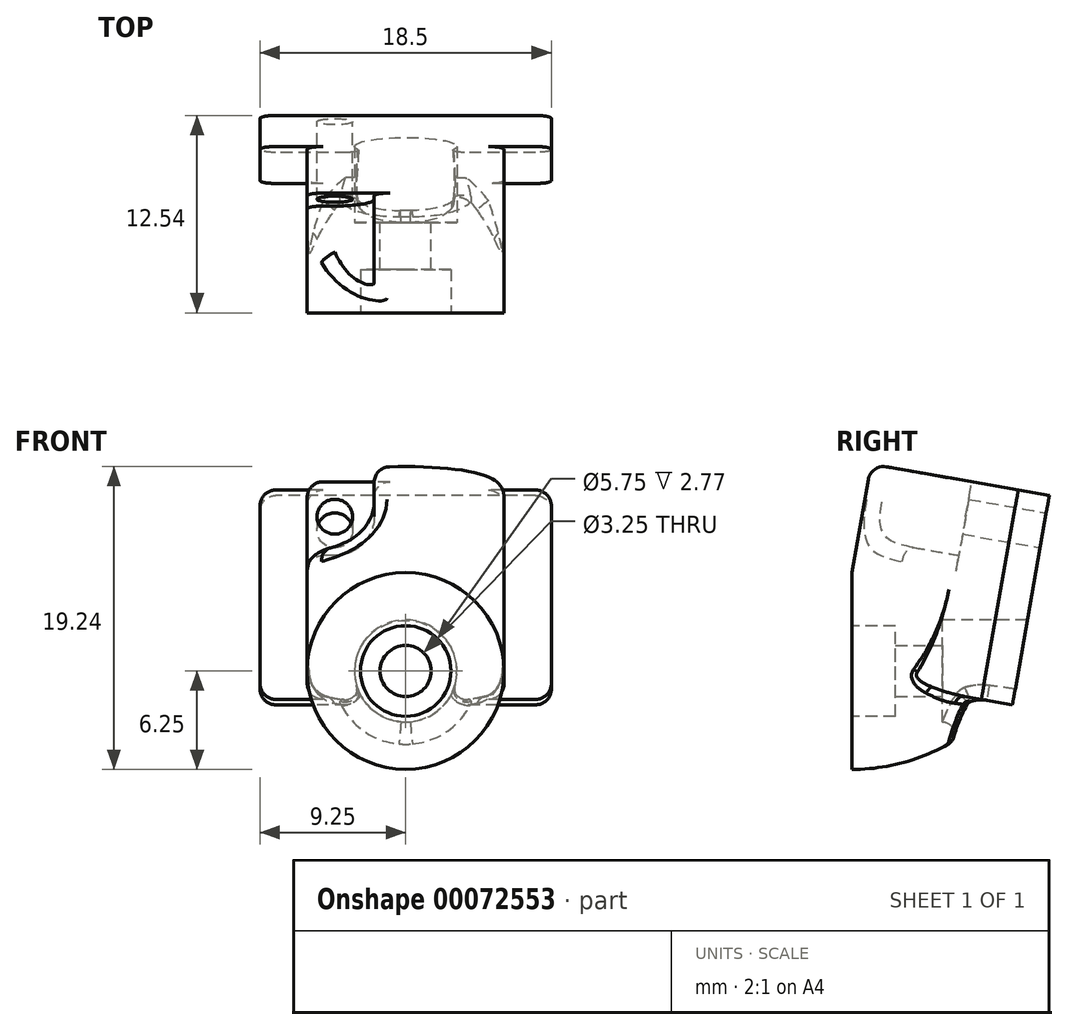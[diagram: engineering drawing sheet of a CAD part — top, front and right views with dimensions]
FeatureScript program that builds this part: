
annotation { "Feature Type Name" : "Feature", "Feature Type Description" : "" }
export const myFeature = defineFeature(function(context is Context, id is Id, definition is map)
    precondition{}
    {
        {
            var Q0;
            Q0=qCreatedBy(makeId("Front.planeOp"),FACE);
            var sketch = newSketch(context, id + "F0", { "sketchPlane" : qUnion([Q0])});
            skCircle(sketch, "E0", {"center": v(0, 0) * mm, "radius": 6.25 * mm});
            skSolve(sketch);
        }
        {
            var Q0;
            Q0=qCreatedBy(makeId("Front.planeOp"),FACE);
            var sketch = newSketch(context, id + "F1", { "sketchPlane" : qUnion([Q0])});
            skLineSegment(sketch, "E1", {"start": v(-10, 6.25) * mm, "end": v(10, 6.25) * mm, "construction": true});
            skLineSegment(sketch, "E2", {"start": v(-10, 6.25) * mm, "end": v(0, 0) * mm, "construction": true});
            skLineSegment(sketch, "E3", {"start": v(0, 0) * mm, "end": v(10, 6.25) * mm, "construction": true});
            skSolve(sketch);
        }
        {
            var Q0;
            Q0=makeQuery(id+"F0.imprint","IMPRINT",FACE,{"disambiguationData":[TD([[makeQuery(id+"F0.imprint","IMPRINT",EDGE,{"derivedFrom":sQuery(id+"F0.wireOp",EDGE,"E0")}),1.0]])]});
            var Q1;
            Q1=sQuery(id+"F1.wireOp",EDGE,"E1");
            revolve(context, id + "F2", {"entities" : qUnion([Q0]), "axis" : qUnion([Q1]), "revolveType" : RevolveType.ONE_DIRECTION, "angle" : 80 * degree});
        }
        {
            var Q0;
            Q0=makeQuery(id+"F2.opRevolve","CAP_FACE",FACE,{"disambiguationData":[OSD([sQuery(id+"F0.wireOp",EDGE,"E0")])],"isStart":false});
            var sketch = newSketch(context, id + "F3", { "sketchPlane" : qUnion([Q0])});
            skCircle(sketch, "E4.0.0", {"center": v(0, 5.16) * mm, "radius": 6.25 * mm});
            skSolve(sketch);
        }
        {
            var Q0;
            Q0=qSketchRegion(id+"F3",true);
            extrude(context, id + "F4", {"entities" : qUnion([Q0]), "operationType" : NewBodyOperationType.ADD, "depth" : 7 * mm});
        }
        {
            var Q0;
            Q0=makeQuery(id+"F4.opExtrude","CAP_FACE",FACE,{"disambiguationData":[OSD([sQuery(id+"F3.wireOp",EDGE,"E4.0.0")])],"isStart":false});
            var sketch = newSketch(context, id + "F5", { "sketchPlane" : qUnion([Q0])});
            skLineSegment(sketch, "E5.bottom", {"start": v(9.25, 8.41) * mm, "end": v(6.25, 8.41) * mm});
            skLineSegment(sketch, "E5.top", {"start": v(9.25, 10.41) * mm, "end": v(-9.25, 10.41) * mm});
            skLineSegment(sketch, "E5.left", {"start": v(9.25, 8.41) * mm, "end": v(9.25, 10.41) * mm});
            skLineSegment(sketch, "E5.right", {"start": v(-9.25, 8.41) * mm, "end": v(-9.25, 10.41) * mm});
            skLineSegment(sketch, "E6.left", {"start": v(6.25, 8.41) * mm, "end": v(6.25, 5.16) * mm});
            skLineSegment(sketch, "E6.right", {"start": v(-6.25, 8.41) * mm, "end": v(-6.25, 5.16) * mm});
            skArc(sketch, "E7", {"start": v(6.25, 5.16) * mm, "mid": v(0, -1.09) * mm, "end": v(-6.25, 5.16) * mm});
            skLineSegment(sketch, "E8.trimOffspring", {"start": v(-6.25, 8.41) * mm, "end": v(-9.25, 8.41) * mm});
            skSolve(sketch);
        }
        {
            var Q0;
            Q0=qSketchRegion(id+"F5",true);
            extrude(context, id + "F6", {"entities" : qUnion([Q0]), "operationType" : NewBodyOperationType.ADD, "oppositeDirection" : true, "depth" : 13.5 * mm});
        }
        {
            var Q0;
            {var subQ4=sQuery(id+"F5.wireOp",EDGE,"E5.right");var subQ6=sQuery(id+"F5.wireOp",EDGE,"E5.top");Q0=makeQuery(id+"F6.boolean.opBoolean","SPLIT",FACE,{"disambiguationData":[TD([makeQuery(id+"F6.opExtrude","SWEPT_FACE",FACE,{"disambiguationData":[OSD([subQ4])]})])],"derivedFrom":makeQuery(id+"F6.opExtrude","SWEPT_FACE",FACE,{"disambiguationData":[OSD([subQ6])]})});}
            var sketch = newSketch(context, id + "F7", { "sketchPlane" : qUnion([Q0])});
            skLineSegment(sketch, "E9.bottom", {"start": v(-20, 16.1) * mm, "end": v(22.94, 16.1) * mm});
            skLineSegment(sketch, "E9.top", {"start": v(-20, -5.87) * mm, "end": v(22.94, -5.87) * mm});
            skLineSegment(sketch, "E9.left", {"start": v(-20, 16.1) * mm, "end": v(-20, -5.87) * mm});
            skLineSegment(sketch, "E9.right", {"start": v(22.94, 16.1) * mm, "end": v(22.94, -5.87) * mm});
            skSolve(sketch);
        }
        {
            var Q0;
            Q0 = qSketchRegion(id + "F7", true);
            extrude(context, id + "F8", {"entities" : qUnion([Q0]), "operationType" : NewBodyOperationType.REMOVE, "depth" : 25 * mm});
        }
        {
            var Q0;
            Q0=makeQuery(id+"F2.opRevolve","CAP_FACE",FACE,{"disambiguationData":[OSD([sQuery(id+"F0.wireOp",EDGE,"E0")])],"isStart":true});
            var sketch = newSketch(context, id + "F9", { "sketchPlane" : qUnion([Q0])});
            skCircle(sketch, "E10.0", {"center": v(0, 0) * mm, "radius": 6.25 * mm});
            skSolve(sketch);
        }
        {
            var Q0;
            Q0=qSketchRegion(id+"F9",true);
            extrude(context, id + "F10", {"entities" : qUnion([Q0]), "operationType" : NewBodyOperationType.REMOVE, "depth" : 25 * mm});
        }
        {
            var Q0;
            Q0=makeQuery(id+"F6.opExtrude","SWEPT_FACE",FACE,{"disambiguationData":[OSD([sQuery(id+"F5.wireOp",EDGE,"E5.top")])]});
            var sketch = newSketch(context, id + "F11", { "sketchPlane" : qUnion([Q0])});
            skCircle(sketch, "E11", {"center": v(-4.5, 10.9) * mm, "radius": 1.13 * mm, "construction": true});
            skEllipse(sketch, "E12.0", {"center": v(0, 0) * mm, "majorRadius": 6.25 * mm, "minorRadius": 6.16 * mm, "majorAxis": v(-1, 0), "construction": true});
            skLineSegment(sketch, "E13", {"start": v(0, 0) * mm, "end": v(0, 18.18) * mm, "construction": true});
            skCircle(sketch, "E14.MirrorC", {"center": v(4.5, 10.9) * mm, "radius": 1.13 * mm});
            skSolve(sketch);
        }
        {
            var Q0;
            Q0=qSketchRegion(id+"F11",true);
            extrude(context, id + "F12", {"entities" : qUnion([Q0]), "operationType" : NewBodyOperationType.REMOVE, "oppositeDirection" : true, "depth" : 25 * mm});
        }
        {
            var Q0;
            Q0=makeQuery(id+"F10.boolean.opBoolean","MERGE",FACE,{"derivedFrom":[makeQuery(id+"F2.opRevolve","CAP_FACE",FACE,{"disambiguationData":[OSD([sQuery(id+"F0.wireOp",EDGE,"E0")])],"isStart":true}),makeQuery(id+"F10.opExtrude","CAP_FACE",FACE,{"disambiguationData":[OSD([sQuery(id+"F9.wireOp",EDGE,"E10.0")])],"isStart":true})]});
            var sketch = newSketch(context, id + "F13", { "sketchPlane" : qUnion([Q0])});
            skCircle(sketch, "E15", {"center": v(0, 0) * mm, "radius": 2.87 * mm});
            skSolve(sketch);
        }
        {
            var Q0;
            Q0=qSketchRegion(id+"F13",true);
            extrude(context, id + "F14", {"entities" : qUnion([Q0]), "operationType" : NewBodyOperationType.REMOVE, "oppositeDirection" : true, "depth" : 2.77 * mm});
        }
        {
            var Q0;
            Q0=makeQuery(id+"F10.boolean.opBoolean","MERGE",FACE,{"derivedFrom":[makeQuery(id+"F2.opRevolve","CAP_FACE",FACE,{"disambiguationData":[OSD([sQuery(id+"F0.wireOp",EDGE,"E0")])],"isStart":true}),makeQuery(id+"F10.opExtrude","CAP_FACE",FACE,{"disambiguationData":[OSD([sQuery(id+"F9.wireOp",EDGE,"E10.0")])],"isStart":true})]});
            cPlane(context, id + "F15", {"entities" : qUnion([Q0]), "cplaneType" : CPlaneType.OFFSET, "offset" : 5.75 * mm, "oppositeDirection" : true, "width" : 150 * mm, "height" : 150 * mm});
        }
        {
            var Q0;
            Q0=qCreatedBy(id+"F15.planeOp",FACE);
            var sketch = newSketch(context, id + "F16", { "sketchPlane" : qUnion([Q0])});
            skCircle(sketch, "E16", {"center": v(0, 0) * mm, "radius": 3.25 * mm});
            skSolve(sketch);
        }
        {
            var Q0;
            Q0=makeQuery(id+"F10.boolean.opBoolean","MERGE",FACE,{"derivedFrom":[makeQuery(id+"F2.opRevolve","CAP_FACE",FACE,{"disambiguationData":[OSD([sQuery(id+"F0.wireOp",EDGE,"E0")])],"isStart":true}),makeQuery(id+"F10.opExtrude","CAP_FACE",FACE,{"disambiguationData":[OSD([sQuery(id+"F9.wireOp",EDGE,"E10.0")])],"isStart":true})]});
            var sketch = newSketch(context, id + "F17", { "sketchPlane" : qUnion([Q0])});
            skLineSegment(sketch, "E17", {"start": v(0, 6.25) * mm, "end": v(16.38, 6.25) * mm});
            skSolve(sketch);
        }
        {
            var Q0;
            Q0=makeQuery(id+"F6.opExtrude","SWEPT_FACE",FACE,{"disambiguationData":[OSD([sQuery(id+"F5.wireOp",EDGE,"E5.top")])]});
            cPlane(context, id + "F18", {"entities" : qUnion([Q0]), "cplaneType" : CPlaneType.OFFSET, "offset" : 5 * mm, "oppositeDirection" : true, "width" : 150 * mm, "height" : 150 * mm});
        }
        {
            var Q0;
            Q0=qCreatedBy(id+"F18.planeOp",FACE);
            var sketch = newSketch(context, id + "F19", { "sketchPlane" : qUnion([Q0])});
            skArc(sketch, "E18", {"start": v(-4.5, 8.4) * mm, "mid": v(-2.73, 9.14) * mm, "end": v(-2, 10.9) * mm, "construction": true});
            skLineSegment(sketch, "E19.bottom", {"start": v(-4.5, 8.4) * mm, "end": v(-12.7, 8.4) * mm, "construction": true});
            skLineSegment(sketch, "E19.top", {"start": v(-2, 17.18) * mm, "end": v(-12.7, 17.18) * mm, "construction": true});
            skLineSegment(sketch, "E19.left", {"start": v(-2, 10.9) * mm, "end": v(-2, 17.18) * mm, "construction": true});
            skLineSegment(sketch, "E19.right", {"start": v(-12.7, 8.4) * mm, "end": v(-12.7, 17.18) * mm, "construction": true});
            skEllipse(sketch, "E20.0", {"center": v(0, 0) * mm, "majorRadius": 2.87 * mm, "minorRadius": 2.83 * mm, "majorAxis": v(-1, 0), "construction": true});
            skLineSegment(sketch, "E21", {"start": v(0, 0) * mm, "end": v(0, 16.32) * mm, "construction": true});
            skLineSegment(sketch, "E22.MirrorCS", {"start": v(12.7, 8.4) * mm, "end": v(12.7, 17.18) * mm});
            skLineSegment(sketch, "E23.MirrorCS", {"start": v(2, 10.9) * mm, "end": v(2, 17.18) * mm});
            skLineSegment(sketch, "E24.MirrorCS", {"start": v(2, 17.18) * mm, "end": v(12.7, 17.18) * mm});
            skLineSegment(sketch, "E25.MirrorCS", {"start": v(4.5, 8.4) * mm, "end": v(12.7, 8.4) * mm});
            skArc(sketch, "E26.MirrorCS", {"start": v(4.5, 8.4) * mm, "mid": v(2.73, 9.14) * mm, "end": v(2, 10.9) * mm});
            skSolve(sketch);
        }
        {
            var Q0;
            Q0=qSketchRegion(id+"F19",true);
            extrude(context, id + "F20", {"entities" : qUnion([Q0]), "operationType" : NewBodyOperationType.REMOVE, "oppositeDirection" : true, "depth" : 25 * mm});
        }
        {
            var Q0;
            Q0=makeQuery(id+"F20.boolean.opBoolean","INTERSECT",EDGE,{"derivedFrom":[makeQuery(id+"F6.boolean.opBoolean","MERGE",FACE,{"derivedFrom":[makeQuery(id+"F4.opExtrude","CAP_FACE",FACE,{"disambiguationData":[OSD([sQuery(id+"F3.wireOp",EDGE,"E4.0.0")])],"isStart":false}),makeQuery(id+"F6.opExtrude","CAP_FACE",FACE,{"disambiguationData":[OSD([sQuery(id+"F5.wireOp",EDGE,"E5.bottom"),sQuery(id+"F5.wireOp",EDGE,"E5.top"),sQuery(id+"F5.wireOp",EDGE,"E5.left"),sQuery(id+"F5.wireOp",EDGE,"E5.right"),sQuery(id+"F5.wireOp",EDGE,"E6.left"),sQuery(id+"F5.wireOp",EDGE,"E6.right"),sQuery(id+"F5.wireOp",EDGE,"E7"),sQuery(id+"F5.wireOp",EDGE,"E8.trimOffspring")])],"isStart":true})]}),makeQuery(id+"F20.opExtrude","SWEPT_FACE",FACE,{"disambiguationData":[OSD([sQuery(id+"F19.wireOp",EDGE,"E23.MirrorCS")])]})]});
            var Q1;
            Q1=makeQuery(id+"F6.opExtrude","CAP_EDGE",EDGE,{"disambiguationData":[OSD([sQuery(id+"F5.wireOp",EDGE,"E6.left")])],"isStart":true});
            var Q2;
            {var subQ3=sQuery(id+"F3.wireOp",EDGE,"E4.0.0");var subQ4=sQuery(id+"F0.wireOp",EDGE,"E0");Q2=makeQuery(id+"F20.boolean.opBoolean","INTERSECT",EDGE,{"derivedFrom":[makeQuery(id+"F6.boolean.opBoolean","SPLIT",FACE,{"disambiguationData":[TD([makeQuery(id+"F2.opRevolve","CAP_FACE",FACE,{"disambiguationData":[OSD([subQ4])],"isStart":true})])],"derivedFrom":makeQuery(id+"F4.opExtrude","SWEPT_FACE",FACE,{"disambiguationData":[OSD([subQ3])]})}),makeQuery(id+"F20.opExtrude","SWEPT_FACE",FACE,{"disambiguationData":[OSD([sQuery(id+"F19.wireOp",EDGE,"E26.MirrorCS")])]})]});}
            var Q3;
            {var subQ3=sQuery(id+"F3.wireOp",EDGE,"E4.0.0");var subQ4=sQuery(id+"F0.wireOp",EDGE,"E0");Q3=makeQuery(id+"F20.boolean.opBoolean","INTERSECT",EDGE,{"derivedFrom":[makeQuery(id+"F6.boolean.opBoolean","SPLIT",FACE,{"disambiguationData":[TD([makeQuery(id+"F2.opRevolve","CAP_FACE",FACE,{"disambiguationData":[OSD([subQ4])],"isStart":true})])],"derivedFrom":makeQuery(id+"F4.opExtrude","SWEPT_FACE",FACE,{"disambiguationData":[OSD([subQ3])]})}),makeQuery(id+"F20.opExtrude","SWEPT_FACE",FACE,{"disambiguationData":[OSD([sQuery(id+"F19.wireOp",EDGE,"E23.MirrorCS")])]})]});}
            var Q4;
            {var subQ3=sQuery(id+"F3.wireOp",EDGE,"E4.0.0");var subQ4=sQuery(id+"F0.wireOp",EDGE,"E0");Q4=makeQuery(id+"F20.boolean.opBoolean","INTERSECT",EDGE,{"derivedFrom":[makeQuery(id+"F6.boolean.opBoolean","SPLIT",FACE,{"disambiguationData":[TD([makeQuery(id+"F2.opRevolve","CAP_FACE",FACE,{"disambiguationData":[OSD([subQ4])],"isStart":true})])],"derivedFrom":makeQuery(id+"F4.opExtrude","SWEPT_FACE",FACE,{"disambiguationData":[OSD([subQ3])]})}),makeQuery(id+"F20.opExtrude","SWEPT_FACE",FACE,{"disambiguationData":[OSD([sQuery(id+"F19.wireOp",EDGE,"E25.MirrorCS")])]})]});}
            var Q5;
            Q5=makeQuery(id+"F6.opExtrude","CAP_EDGE",EDGE,{"disambiguationData":[OSD([sQuery(id+"F5.wireOp",EDGE,"E5.right")])],"isStart":true});
            var Q6;
            Q6=makeQuery(id+"F6.opExtrude","CAP_EDGE",EDGE,{"disambiguationData":[OSD([sQuery(id+"F5.wireOp",EDGE,"E5.left")])],"isStart":true});
            var Q7;
            Q7=makeQuery(id+"F6.opExtrude","CAP_EDGE",EDGE,{"disambiguationData":[OSD([sQuery(id+"F5.wireOp",EDGE,"E6.right")])],"isStart":false});
            var Q8;
            Q8=makeQuery(id+"F6.opExtrude","CAP_EDGE",EDGE,{"disambiguationData":[OSD([sQuery(id+"F5.wireOp",EDGE,"E6.left")])],"isStart":false});
            var Q9;
            Q9=makeQuery(id+"F6.opExtrude","CAP_EDGE",EDGE,{"disambiguationData":[OSD([sQuery(id+"F5.wireOp",EDGE,"E5.right")])],"isStart":false});
            var Q10;
            Q10=makeQuery(id+"F6.opExtrude","CAP_EDGE",EDGE,{"disambiguationData":[OSD([sQuery(id+"F5.wireOp",EDGE,"E5.left")])],"isStart":false});
            var Q11;
            Q11=makeQuery(id+"F6.opExtrude","CAP_EDGE",EDGE,{"disambiguationData":[OSD([sQuery(id+"F5.wireOp",EDGE,"E6.right")])],"isStart":true});
            fillet(context, id + "F21", {"entities" : qUnion([Q0, Q1, Q2, Q3, Q4, Q5, Q6, Q7, Q8, Q9, Q10, Q11]), "radius" : 1 * mm, "tangentPropagation" : true, "allowEdgeOverflow" : false});
        }
        {
            var Q0;
            Q0=qSketchRegion(id+"F16",true);
            extrude(context, id + "F22", {"entities" : qUnion([Q0]), "operationType" : NewBodyOperationType.REMOVE, "oppositeDirection" : true, "depth" : 25 * mm});
        }
        {
            var Q0;
            Q0=makeQuery(id+"F22.boolean.opBoolean","COPY",FACE,{"derivedFrom":makeQuery(id+"F22.opExtrude","CAP_FACE",FACE,{"disambiguationData":[OSD([sQuery(id+"F16.wireOp",EDGE,"E16")])],"isStart":true})});
            var sketch = newSketch(context, id + "F23", { "sketchPlane" : qUnion([Q0])});
            skCircle(sketch, "E27", {"center": v(0, 0) * mm, "radius": 1.63 * mm});
            skSolve(sketch);
        }
        {
            var Q0;
            Q0=qSketchRegion(id+"F23",true);
            extrude(context, id + "F24", {"entities" : qUnion([Q0]), "operationType" : NewBodyOperationType.REMOVE, "oppositeDirection" : true, "depth" : 25 * mm});
        }
        {
            var Q0;
            Q0=makeQuery(id+"F6.boolean.opBoolean","INTERSECT",EDGE,{"disambiguationData":[OD(1.0)],"derivedFrom":[makeQuery(id+"F2.opRevolve","SWEPT_FACE",FACE,{"disambiguationData":[OSD([sQuery(id+"F0.wireOp",EDGE,"E0")])]}),makeQuery(id+"F6.opExtrude","SWEPT_FACE",FACE,{"disambiguationData":[OSD([sQuery(id+"F5.wireOp",EDGE,"E7")])]})]});
            var Q1;
            Q1=makeQuery(id+"F6.boolean.opBoolean","INTERSECT",EDGE,{"disambiguationData":[OD(0.0)],"derivedFrom":[makeQuery(id+"F2.opRevolve","SWEPT_FACE",FACE,{"disambiguationData":[OSD([sQuery(id+"F0.wireOp",EDGE,"E0")])]}),makeQuery(id+"F6.opExtrude","SWEPT_FACE",FACE,{"disambiguationData":[OSD([sQuery(id+"F5.wireOp",EDGE,"E7")])]})]});
            fillet(context, id + "F25", {"entities" : qUnion([Q0, Q1]), "radius" : 1 * mm, "tangentPropagation" : true, "allowEdgeOverflow" : false});
        }
        {
            var Q0;
            {var subQ0=sQuery(id+"F5.wireOp",EDGE,"E5.left");var subQ1=sQuery(id+"F5.wireOp",EDGE,"E5.bottom");var subQ2=sQuery(id+"F5.wireOp",EDGE,"E5.right");var subQ3=sQuery(id+"F5.wireOp",EDGE,"E5.top");var subQ4=sQuery(id+"F5.wireOp",EDGE,"E6.left");var subQ5=sQuery(id+"F5.wireOp",EDGE,"E6.right");var subQ6=sQuery(id+"F5.wireOp",EDGE,"E7");var subQ7=sQuery(id+"F5.wireOp",EDGE,"E8.trimOffspring");Q0=makeQuery(id+"F22.boolean.opBoolean","INTERSECT",EDGE,{"disambiguationData":[OD(0.0)],"derivedFrom":[makeQuery(id+"F6.boolean.opBoolean","SPLIT",FACE,{"disambiguationData":[TD([makeQuery(id+"F2.opRevolve","SWEPT_FACE",FACE,{"disambiguationData":[OSD([sQuery(id+"F0.wireOp",EDGE,"E0")])]})])],"derivedFrom":makeQuery(id+"F6.opExtrude","CAP_FACE",FACE,{"disambiguationData":[OSD([subQ1,subQ3,subQ0,subQ2,subQ4,subQ5,subQ6,subQ7])],"isStart":false})}),makeQuery(id+"F22.opExtrude","SWEPT_FACE",FACE,{"disambiguationData":[OSD([sQuery(id+"F16.wireOp",EDGE,"E16")])]})]});}
            fillet(context, id + "F26", {"entities" : qUnion([Q0]), "radius" : 0.75 * mm, "tangentPropagation" : true, "allowEdgeOverflow" : false});
        }
    });
